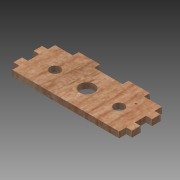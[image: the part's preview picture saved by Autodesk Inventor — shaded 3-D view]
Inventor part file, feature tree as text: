
AUTODESK INVENTOR PART (.ipt)
format: ipt  version: 2015 (Build 190159000, 159)  size: 298,496 bytes
history: native  units: mm
features: other x14, sketch x10, extrude x3, hole x2
ambient origin geometry x8: Origin, YZ Plane, XZ Plane, XY Plane, X Axis, Y Axis, Z Axis, Center Point
bodies: Body1 (feature_tree)
feature tree (29):
  other  "Blocks"
  extrude  "Extrusion2"  Depth=40.0mm
  hole  "Hole5"  [1 undecoded]
  sketch  "Sketch17"  dims[d53=9.6mm d54=6.0mm d55=4.0mm d56=2.0mm d57=90.0deg d58=4.0mm d59=0.0mm]
  hole  "Hole14"  [1 undecoded]
  extrude  "Extrusion4"  Depth=5.5mm
  extrude  "Extrusion5"  Depth=6.666667mm
  sketch  "Sketch46"  dims[d140=20.0mm]
  sketch  "Sketch47"  dims[d141=4.0mm d142=16.666667mm d143=20.0mm d144=5.5mm d145=5.5mm d146=0.0mm d29=1.0mm d30=1.0mm]
  sketch  "Sketch44"  dims[d138=5.5mm]
  sketch  "Sketch45"  dims[d139=0.0mm]
  sketch  "Sketch43"  dims[d134=8.0mm d135=6.666667mm]
  sketch  "Sketch10"  dims[d21=100.0mm d22=40.0mm]
  sketch  "Sketch16"  dims[d23=5.5mm d24=0.0mm d52=60.0mm]
  sketch  "Sketch34"  dims[d122=14.0mm d123=6.0mm d124=4.0mm d125=2.0mm d126=90.0deg d127=89.0mm d128=20.594885mm d131=20.0mm]
  sketch  "Sketch35"  dims[d132=5.5mm d133=5.5mm]
  other  "Block1"
  other  "Block2"
  other  "Block3"
  other  "Block4"
  other  "Block5"
  other  "Block6"
  other  "Block7"
  other  "Block5:1"
  other  "Block5:2"
  other  "Block6:1"
  other  "Block6:2"
  other  "Block7:1"
  other  "Block7:2"
note: 2 required parameter values undecoded (feature->parameter linkage not recoverable at this tier; creation-order binding heuristic only, values carry confidence <= 0.55)
